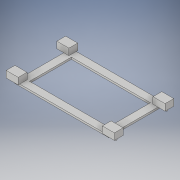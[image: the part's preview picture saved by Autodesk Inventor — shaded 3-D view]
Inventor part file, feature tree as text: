
AUTODESK INVENTOR PART (.ipt)
format: ipt  version: 2018 (Build 220112000, 112)  size: 161,280 bytes
history: native  units: mm
features: extrude x3, sketch x3
ambient origin geometry x8: Origin, YZ Plane, XZ Plane, XY Plane, X Axis, Y Axis, Z Axis, Center Point
bodies: Solid1 (feature_tree)
feature tree (6):
  extrude  "Extrusion1"  Depth=225.0mm
  extrude  "Extrusion2"  Depth=7.5mm TaperAngle=0.0deg
  extrude  "Extrusion3"  Depth=35.0mm
  sketch  "Sketch1"  dims[d0=375.0mm d1=225.0mm]
  sketch  "Sketch2"  dims[d2=315.0mm d3=7.5mm d4=0.0mm]
  sketch  "Sketch3"  dims[d5=10.0mm d6=35.0mm d7=48.0mm d8=35.0mm d9=10.0mm d10=48.0mm d11=35.0mm d12=10.0mm d13=48.0mm d14=35.0mm d15=48.0mm d16=10.0mm d17=48.0mm d18=35.0mm d19=48.0mm d20=26.0mm d21=0.0mm d24=8.0mm d30=8.0mm d31=100.893733mm d32=203.5mm d33=203.5mm d34=100.893733mm d35=100.893733mm d36=203.5mm d37=100.893733mm d38=203.5mm d39=12.0mm d40=0.0mm]
